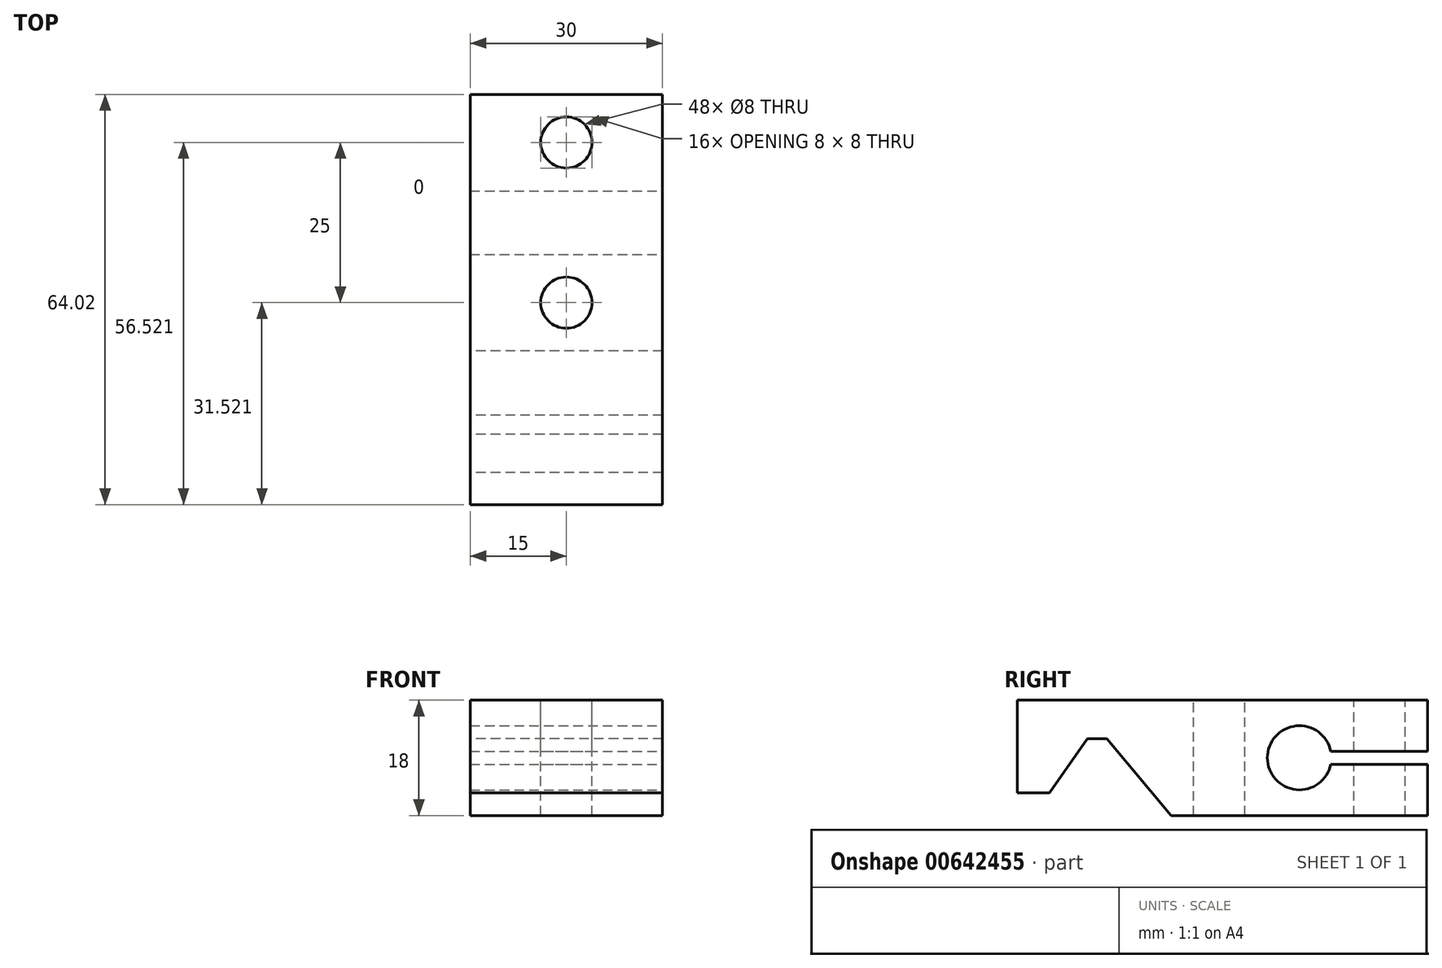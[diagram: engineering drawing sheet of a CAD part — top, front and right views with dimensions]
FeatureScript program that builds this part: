
annotation { "Feature Type Name" : "Feature", "Feature Type Description" : "" }
export const myFeature = defineFeature(function(context is Context, id is Id, definition is map)
    precondition{}
    {
        {
            var Q0;
            Q0=qCreatedBy(makeId("Right.planeOp"),FACE);
            var sketch = newSketch(context, id + "F0", { "sketchPlane" : qUnion([Q0])});
            skLineSegment(sketch, "E0", {"start": v(24.02, 8.94) * mm, "end": v(13.95, 20.94) * mm});
            skLineSegment(sketch, "E1", {"start": v(13.95, 20.94) * mm, "end": v(10.95, 20.94) * mm});
            skLineSegment(sketch, "E2", {"start": v(10.95, 20.94) * mm, "end": v(5, 12.44) * mm});
            skLineSegment(sketch, "E3", {"start": v(5, 12.44) * mm, "end": v(0, 12.44) * mm});
            skLineSegment(sketch, "E4", {"start": v(0, 12.44) * mm, "end": v(0, 26.94) * mm});
            skLineSegment(sketch, "E5", {"start": v(0, 26.94) * mm, "end": v(64.02, 26.94) * mm});
            skLineSegment(sketch, "E6", {"start": v(24.02, 8.94) * mm, "end": v(64.02, 8.94) * mm});
            skLineSegment(sketch, "E7", {"start": v(64.02, 8.94) * mm, "end": v(64.02, 26.94) * mm});
            skSolve(sketch);
        }
        {
            var Q0;
            Q0=makeQuery(id+"F0.imprint","IMPRINT",FACE,{"disambiguationData":[TD([[makeQuery(id+"F0.imprint","IMPRINT",EDGE,{"derivedFrom":sQuery(id+"F0.wireOp",EDGE,"HQAWHFrx-uIpa-Nd3d-1sSg-BDlqojRyJbRw")}),-1.0]])]});
            var Q1;
            Q1=makeQuery(id+"F0.imprint","IMPRINT",FACE,{"disambiguationData":[TD([[makeQuery(id+"F0.imprint","IMPRINT",EDGE,{"derivedFrom":sQuery(id+"F0.wireOp",EDGE,"E0")}),-1.0]])]});
            extrude(context, id + "F1", {"entities" : qUnion([Q0, Q1]), "depth" : 30 * mm, "offsetDistance" : 25 * mm});
        }
        {
            var Q0;
            Q0=makeQuery(id+"F1.opExtrude","CAP_FACE",FACE,{"disambiguationData":[OSD([sQuery(id+"F0.wireOp",EDGE,"HQAWHFrx-uIpa-Nd3d-1sSg-BDlqojRyJbRw"),sQuery(id+"F0.wireOp",EDGE,"E0"),sQuery(id+"F0.wireOp",EDGE,"E1"),sQuery(id+"F0.wireOp",EDGE,"E2"),sQuery(id+"F0.wireOp",EDGE,"E3"),sQuery(id+"F0.wireOp",EDGE,"E4"),sQuery(id+"F0.wireOp",EDGE,"E5"),sQuery(id+"F0.wireOp",EDGE,"xRuK4pUl-k4Ka-OoXQ-0Vtm-nTqqHO9WyQdM"),sQuery(id+"F0.wireOp",EDGE,"6cQgLwex-22rI-TnAo-ivrf-HJUvyfB4cz5s")])],"isStart":false});
            var sketch = newSketch(context, id + "F2", { "sketchPlane" : qUnion([Q0])});
            skCircle(sketch, "E8", {"center": v(44.02, 17.94) * mm, "radius": 5 * mm});
            skSolve(sketch);
        }
        {
            var Q0;
            Q0=makeQuery(id+"F2.imprint","IMPRINT",FACE,{"disambiguationData":[TD([[makeQuery(id+"F2.imprint","IMPRINT",EDGE,{"derivedFrom":sQuery(id+"F2.wireOp",EDGE,"E8")}),-1.0]])]});
            var sketch = newSketch(context, id + "F3", { "sketchPlane" : qUnion([Q0])});
            skLineSegment(sketch, "E9.bottom", {"start": v(46.9, 16.94) * mm, "end": v(66.54, 16.94) * mm});
            skLineSegment(sketch, "E9.top", {"start": v(46.9, 18.94) * mm, "end": v(66.54, 18.94) * mm});
            skLineSegment(sketch, "E9.left", {"start": v(46.9, 16.94) * mm, "end": v(46.9, 18.94) * mm});
            skLineSegment(sketch, "E9.right", {"start": v(66.54, 16.94) * mm, "end": v(66.54, 18.94) * mm});
            skLineSegment(sketch, "E10", {"start": v(49.15, 17.94) * mm, "end": v(65.3, 17.94) * mm, "construction": true});
            skSolve(sketch);
        }
        {
            var Q0;
            Q0 = qSketchRegion(id + "F3", true);
            extrude(context, id + "F4", {"entities" : qUnion([Q0]), "operationType" : NewBodyOperationType.REMOVE, "endBound" : BoundingType.THROUGH_ALL, "oppositeDirection" : true, "depth" : 25 * mm, "offsetDistance" : 25 * mm});
        }
        {
            var Q0;
            Q0=makeQuery(id+"F2.imprint","IMPRINT",FACE,{"disambiguationData":[TD([[makeQuery(id+"F2.imprint","IMPRINT",EDGE,{"derivedFrom":sQuery(id+"F2.wireOp",EDGE,"E8")}),1.0]])]});
            extrude(context, id + "F5", {"entities" : qUnion([Q0]), "operationType" : NewBodyOperationType.REMOVE, "endBound" : BoundingType.THROUGH_ALL, "oppositeDirection" : true, "depth" : 25 * mm, "offsetDistance" : 25 * mm});
        }
        {
            var Q0;
            Q0=makeQuery(id+"F1.opExtrude","SWEPT_FACE",FACE,{"disambiguationData":[OSD([sQuery(id+"F0.wireOp",EDGE,"E5")])]});
            var sketch = newSketch(context, id + "F6", { "sketchPlane" : qUnion([Q0])});
            skLineSegment(sketch, "E11", {"start": v(15, 0) * mm, "end": v(15, 0) * mm});
            skCircle(sketch, "E12", {"center": v(15, 31.52) * mm, "radius": 4 * mm});
            skCircle(sketch, "E13", {"center": v(15, 56.52) * mm, "radius": 4 * mm});
            skPoint(sketch, "E14", {"position": v(15, 64.02) * mm});
            skSolve(sketch);
        }
        {
            var Q0;
            Q0=makeQuery(id+"F6.imprint","IMPRINT",FACE,{"disambiguationData":[TD([[makeQuery(id+"F6.imprint","IMPRINT",EDGE,{"derivedFrom":sQuery(id+"F6.wireOp",EDGE,"E12")}),1.0]])]});
            var Q1;
            Q1=makeQuery(id+"F6.imprint","IMPRINT",FACE,{"disambiguationData":[TD([[makeQuery(id+"F6.imprint","IMPRINT",EDGE,{"derivedFrom":sQuery(id+"F6.wireOp",EDGE,"E13")}),1.0]])]});
            extrude(context, id + "F7", {"entities" : qUnion([Q0, Q1]), "operationType" : NewBodyOperationType.REMOVE, "endBound" : BoundingType.THROUGH_ALL, "oppositeDirection" : true, "depth" : 25 * mm, "offsetDistance" : 25 * mm});
        }
        {
            var Q0;
            Q0 = qSketchRegion(id + "F2", true);
            extrude(context, id + "F8", {"entities" : qUnion([Q0]), "operationType" : NewBodyOperationType.REMOVE, "endBound" : BoundingType.THROUGH_ALL, "oppositeDirection" : true, "depth" : 25 * mm, "offsetDistance" : 25 * mm});
        }
    });
